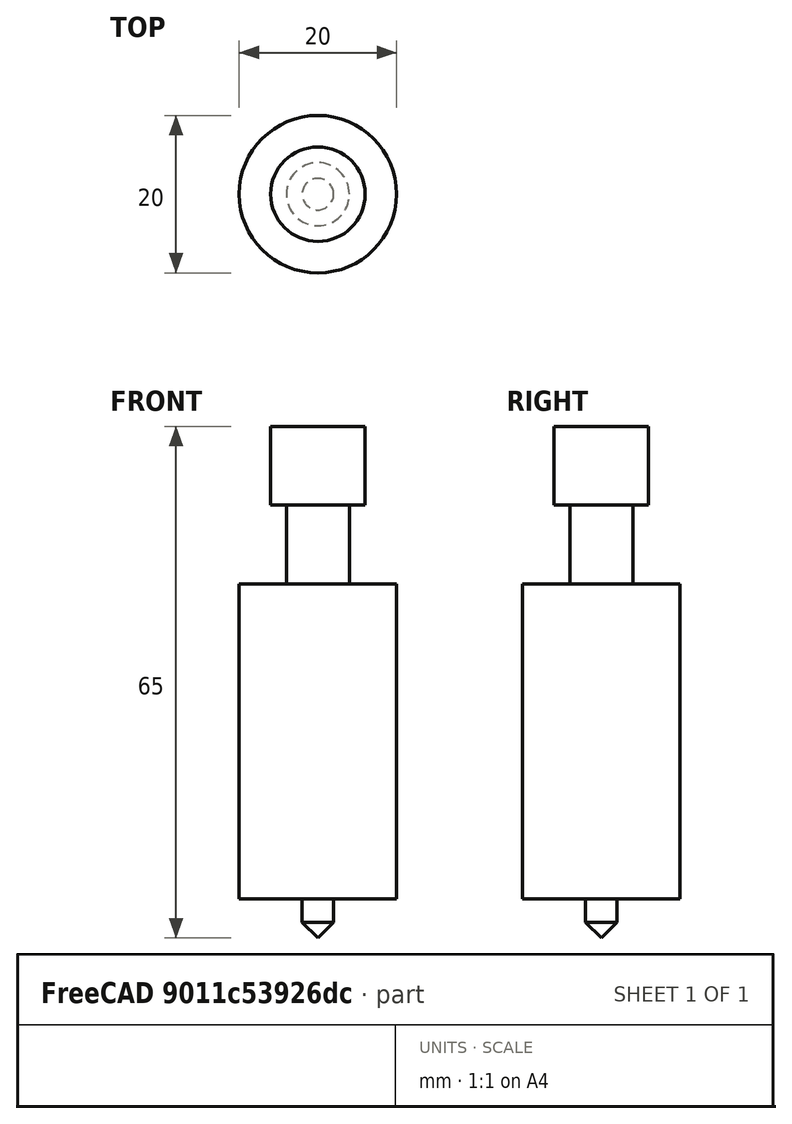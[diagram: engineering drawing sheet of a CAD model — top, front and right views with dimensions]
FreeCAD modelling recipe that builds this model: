
FCSTD DOCUMENT  (FreeCAD 0.18R14555 (Git shallow))
Label: hotend
License: All rights reserved
LicenseURL: http://en.wikipedia.org/wiki/All_rights_reserved
objects: Sketcher::SketchObject×1, PartDesign::Revolution×1, PartDesign::Body×1
note: 4 computed .brp shape members not serialized (recipe doc carries the construction recipe); baked Part::Feature solids carry a one-line shape summary decoded from their .brp

FEATURE [Sketcher::SketchObject] Sketch
  MapMode = 5
  Placement = pos=(0,0,0) rot=(1,0,0;1.5708rad)
  Support = -> [XZ_Plane]
  sketch-geometry (10):
    g0: LineSegment StartX=0 StartY=0 StartZ=0 EndX=2 EndY=2 EndZ=0
    g1: LineSegment StartX=2 StartY=2 StartZ=0 EndX=2 EndY=5 EndZ=0
    g2: LineSegment StartX=2 StartY=5 StartZ=0 EndX=10 EndY=5 EndZ=0
    g3: LineSegment StartX=10 StartY=5 StartZ=0 EndX=10 EndY=45 EndZ=0
    g4: LineSegment StartX=10 StartY=45 StartZ=0 EndX=4 EndY=45 EndZ=0
    g5: LineSegment StartX=4 StartY=45 StartZ=0 EndX=4 EndY=55 EndZ=0
    g6: LineSegment StartX=4 StartY=55 StartZ=0 EndX=6 EndY=55 EndZ=0
    g7: LineSegment StartX=6 StartY=55 StartZ=0 EndX=6 EndY=65 EndZ=0
    g8: LineSegment StartX=6 StartY=65 StartZ=0 EndX=0 EndY=65 EndZ=0
    g9: LineSegment StartX=0 StartY=65 StartZ=0 EndX=0 EndY=0 EndZ=0
  constraints (29):
    c: Coincident(g0,g1)
    c: Vertical(g1)
    c: Coincident(g1,g2)
    c: Horizontal(g2)
    c: Coincident(g2,g3)
    c: Vertical(g3)
    c: Coincident(g3,g4)
    c: Horizontal(g4)
    c: Coincident(g4,g5)
    c: Vertical(g5)
    c: Coincident(g5,g6)
    c: Horizontal(g6)
    c: Coincident(g6,g7)
    c: Vertical(g7)
    c: Coincident(g7,g8)
    c: Horizontal(g8)
    c: Coincident(g8,g9)
    c: Coincident(g9,g0)
    c: Vertical(g9)
    c: DistanceX(g8,g8) = 6
    c: DistanceY(g7,g7) = 10
    c: Coincident(g0,g-1)
    c: DistanceX(g5) = 4
    c: DistanceX(g0) = 2
    c: DistanceY(g1,g1) = 3
    c: DistanceY(g0,g1) = 5
    c: DistanceX(g0,g2) = 10
    c: DistanceY(g0,g6) = 55
    c: DistanceY(g3,g3) = 40
FEATURE [PartDesign::Revolution] Revolution
  Angle = 360
  Axis = (0,2e-16,1)
  Base = (0,0,0)
  Placement = pos=(0,0,0) rot=(1,0,0;1.5708rad)
  Profile = -> Sketch
  ReferenceAxis = -> Sketch [V_Axis]
  Reversed = true
FEATURE [PartDesign::Body] Body
  Group = -> [Sketch,Revolution]
  Origin = -> Origin
  Tip = -> Revolution
